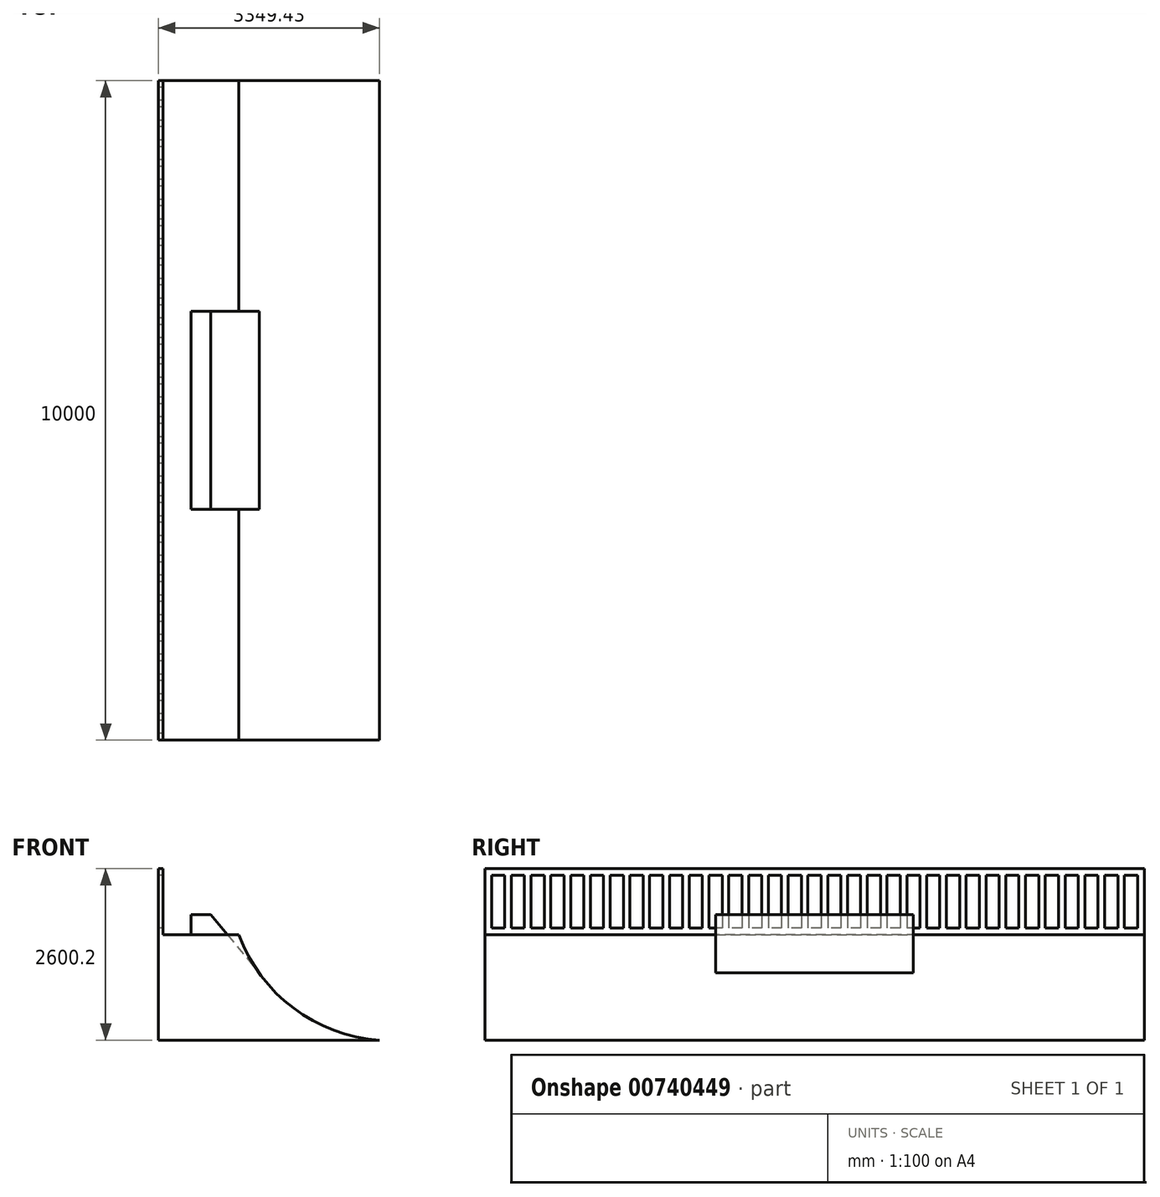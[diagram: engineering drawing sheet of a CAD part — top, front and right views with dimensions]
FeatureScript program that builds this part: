
annotation { "Feature Type Name" : "Feature", "Feature Type Description" : "" }
export const myFeature = defineFeature(function(context is Context, id is Id, definition is map)
    precondition{}
    {
        {
            var Q0;
            Q0=qCreatedBy(makeId("Top.planeOp"),FACE);
            var sketch = newSketch(context, id + "F0", { "sketchPlane" : qUnion([Q0])});
            skLineSegment(sketch, "E0.bottom", {"start": v(5000, 5000) * mm, "end": v(-5000, 5000) * mm, "construction": true});
            skLineSegment(sketch, "E0.top", {"start": v(5000, -5000) * mm, "end": v(-5000, -5000) * mm, "construction": true});
            skLineSegment(sketch, "E0.left", {"start": v(5000, 5000) * mm, "end": v(5000, -5000) * mm, "construction": true});
            skLineSegment(sketch, "E0.right", {"start": v(-5000, 5000) * mm, "end": v(-5000, -5000) * mm});
            skPoint(sketch, "E0.middle", {"position": v(0, 0) * mm});
            skLineSegment(sketch, "E1", {"start": v(-3780.8, 5000) * mm, "end": v(-3780.8, -5000) * mm});
            skLineSegment(sketch, "E2", {"start": v(-3780.8, -5000) * mm, "end": v(-5000, -5000) * mm});
            skLineSegment(sketch, "E3", {"start": v(-3780.8, 5000) * mm, "end": v(-5000, 5000) * mm});
            skSolve(sketch);
        }
        {
            var Q0;
            Q0=makeQuery(id+"F0.imprint","IMPRINT",FACE,{"disambiguationData":[TD([[makeQuery(id+"F0.imprint","IMPRINT",EDGE,{"derivedFrom":sQuery(id+"F0.wireOp",EDGE,"E0.right")}),1.0]])]});
            extrude(context, id + "F1", {"entities" : qUnion([Q0]), "depth" : 1600.2 * mm, "offsetDistance" : 25 * mm});
        }
        {
            var Q0;
            Q0=makeQuery(id+"F1.opExtrude","SWEPT_FACE",FACE,{"disambiguationData":[OSD([sQuery(id+"F0.wireOp",EDGE,"E2")])]});
            var sketch = newSketch(context, id + "F2", { "sketchPlane" : qUnion([Q0])});
            skLineSegment(sketch, "E4.0", {"start": v(-3780.8, 1600.2) * mm, "end": v(-3780.8, 0) * mm});
            skLineSegment(sketch, "E5", {"start": v(-3780.8, 0) * mm, "end": v(-365.8, 0) * mm});
            skLineSegment(sketch, "E6", {"start": v(-3994.4, 2438.4) * mm, "end": v(213.94, 2438.4) * mm, "construction": true});
            skArc(sketch, "E7", {"start": v(-3780.8, 1600.2) * mm, "mid": v(-2821.2, 390.7) * mm, "end": v(-1327.5, 0) * mm});
            skLineSegment(sketch, "E8", {"start": v(-3780.8, 1600.2) * mm, "end": v(-3655.75, 1314.5) * mm, "construction": true});
            skLineSegment(sketch, "E9.0", {"start": v(-3780.8, 1600.2) * mm, "end": v(-5000, 1600.2) * mm});
            skSolve(sketch);
        }
        {
            var Q0;
            {var subQ0=sQuery(id+"F2.wireOp",EDGE,"E4.0");Q0=makeQuery(id+"F2.imprint","IMPRINT",FACE,{"disambiguationData":[TD([[makeQuery(id+"F2.imprint","IMPRINT",EDGE,{"derivedFrom":subQ0}),1.0]])]});}
            var Q1;
            Q1=makeQuery(id+"F1.opExtrude","CAP_EDGE",EDGE,{"disambiguationData":[OSD([sQuery(id+"F0.wireOp",EDGE,"E1")])],"isStart":false});
            sweep(context, id + "F3", {"operationType" : NewBodyOperationType.ADD, "profiles" : qUnion([Q0]), "path" : qUnion([Q1])});
        }
        {
            var Q0;
            Q0=makeQuery(id+"F1.opExtrude","SWEPT_FACE",FACE,{"disambiguationData":[OSD([sQuery(id+"F0.wireOp",EDGE,"E0.right")])]});
            var sketch = newSketch(context, id + "F4", { "sketchPlane" : qUnion([Q0])});
            skLineSegment(sketch, "E10.0", {"start": v(-5000, 1600.2) * mm, "end": v(5000, 1600.2) * mm});
            skLineSegment(sketch, "E11.top", {"start": v(-5000, 2600.2) * mm, "end": v(5000, 2600.2) * mm});
            skLineSegment(sketch, "E11.left", {"start": v(-5000, 1600.2) * mm, "end": v(-5000, 2600.2) * mm});
            skLineSegment(sketch, "E11.right", {"start": v(5000, 1600.2) * mm, "end": v(5000, 2600.2) * mm});
            skLineSegment(sketch, "E12.bottom", {"start": v(-4900, 2500.2) * mm, "end": v(-4700, 2500.2) * mm});
            skLineSegment(sketch, "E12.top", {"start": v(-4900, 1700.2) * mm, "end": v(-4700, 1700.2) * mm});
            skLineSegment(sketch, "E12.left", {"start": v(-4900, 2500.2) * mm, "end": v(-4900, 1700.2) * mm});
            skLineSegment(sketch, "E12.right", {"start": v(-4700, 2500.2) * mm, "end": v(-4700, 1700.2) * mm});
            skLineSegment(sketch, "E13.1.0.0", {"start": v(-4400, 2500.2) * mm, "end": v(-4400, 1700.2) * mm});
            skLineSegment(sketch, "E13.1.0.1", {"start": v(-4600, 2500.2) * mm, "end": v(-4400, 2500.2) * mm});
            skLineSegment(sketch, "E13.1.0.2", {"start": v(-4600, 2500.2) * mm, "end": v(-4600, 1700.2) * mm});
            skLineSegment(sketch, "E13.1.0.3", {"start": v(-4600, 1700.2) * mm, "end": v(-4400, 1700.2) * mm});
            skLineSegment(sketch, "E13.2.0.0", {"start": v(-4100, 2500.2) * mm, "end": v(-4100, 1700.2) * mm});
            skLineSegment(sketch, "E13.2.0.1", {"start": v(-4300, 2500.2) * mm, "end": v(-4100, 2500.2) * mm});
            skLineSegment(sketch, "E13.2.0.2", {"start": v(-4300, 2500.2) * mm, "end": v(-4300, 1700.2) * mm});
            skLineSegment(sketch, "E13.2.0.3", {"start": v(-4300, 1700.2) * mm, "end": v(-4100, 1700.2) * mm});
            skLineSegment(sketch, "E13.3.0.0", {"start": v(-3800, 2500.2) * mm, "end": v(-3800, 1700.2) * mm});
            skLineSegment(sketch, "E13.3.0.1", {"start": v(-4000, 2500.2) * mm, "end": v(-3800, 2500.2) * mm});
            skLineSegment(sketch, "E13.3.0.2", {"start": v(-4000, 2500.2) * mm, "end": v(-4000, 1700.2) * mm});
            skLineSegment(sketch, "E13.3.0.3", {"start": v(-4000, 1700.2) * mm, "end": v(-3800, 1700.2) * mm});
            skLineSegment(sketch, "E13.4.0.0", {"start": v(-3500, 2500.2) * mm, "end": v(-3500, 1700.2) * mm});
            skLineSegment(sketch, "E13.4.0.1", {"start": v(-3700, 2500.2) * mm, "end": v(-3500, 2500.2) * mm});
            skLineSegment(sketch, "E13.4.0.2", {"start": v(-3700, 2500.2) * mm, "end": v(-3700, 1700.2) * mm});
            skLineSegment(sketch, "E13.4.0.3", {"start": v(-3700, 1700.2) * mm, "end": v(-3500, 1700.2) * mm});
            skLineSegment(sketch, "E13.5.0.0", {"start": v(-3200, 2500.2) * mm, "end": v(-3200, 1700.2) * mm});
            skLineSegment(sketch, "E13.5.0.1", {"start": v(-3400, 2500.2) * mm, "end": v(-3200, 2500.2) * mm});
            skLineSegment(sketch, "E13.5.0.2", {"start": v(-3400, 2500.2) * mm, "end": v(-3400, 1700.2) * mm});
            skLineSegment(sketch, "E13.5.0.3", {"start": v(-3400, 1700.2) * mm, "end": v(-3200, 1700.2) * mm});
            skLineSegment(sketch, "E13.6.0.0", {"start": v(-2900, 2500.2) * mm, "end": v(-2900, 1700.2) * mm});
            skLineSegment(sketch, "E13.6.0.1", {"start": v(-3100, 2500.2) * mm, "end": v(-2900, 2500.2) * mm});
            skLineSegment(sketch, "E13.6.0.2", {"start": v(-3100, 2500.2) * mm, "end": v(-3100, 1700.2) * mm});
            skLineSegment(sketch, "E13.6.0.3", {"start": v(-3100, 1700.2) * mm, "end": v(-2900, 1700.2) * mm});
            skLineSegment(sketch, "E13.7.0.0", {"start": v(-2600, 2500.2) * mm, "end": v(-2600, 1700.2) * mm});
            skLineSegment(sketch, "E13.7.0.1", {"start": v(-2800, 2500.2) * mm, "end": v(-2600, 2500.2) * mm});
            skLineSegment(sketch, "E13.7.0.2", {"start": v(-2800, 2500.2) * mm, "end": v(-2800, 1700.2) * mm});
            skLineSegment(sketch, "E13.7.0.3", {"start": v(-2800, 1700.2) * mm, "end": v(-2600, 1700.2) * mm});
            skLineSegment(sketch, "E13.8.0.0", {"start": v(-2300, 2500.2) * mm, "end": v(-2300, 1700.2) * mm});
            skLineSegment(sketch, "E13.8.0.1", {"start": v(-2500, 2500.2) * mm, "end": v(-2300, 2500.2) * mm});
            skLineSegment(sketch, "E13.8.0.2", {"start": v(-2500, 2500.2) * mm, "end": v(-2500, 1700.2) * mm});
            skLineSegment(sketch, "E13.8.0.3", {"start": v(-2500, 1700.2) * mm, "end": v(-2300, 1700.2) * mm});
            skLineSegment(sketch, "E13.9.0.0", {"start": v(-2000, 2500.2) * mm, "end": v(-2000, 1700.2) * mm});
            skLineSegment(sketch, "E13.9.0.1", {"start": v(-2200, 2500.2) * mm, "end": v(-2000, 2500.2) * mm});
            skLineSegment(sketch, "E13.9.0.2", {"start": v(-2200, 2500.2) * mm, "end": v(-2200, 1700.2) * mm});
            skLineSegment(sketch, "E13.9.0.3", {"start": v(-2200, 1700.2) * mm, "end": v(-2000, 1700.2) * mm});
            skLineSegment(sketch, "E13.10.0.0", {"start": v(-1700, 2500.2) * mm, "end": v(-1700, 1700.2) * mm});
            skLineSegment(sketch, "E13.10.0.1", {"start": v(-1900, 2500.2) * mm, "end": v(-1700, 2500.2) * mm});
            skLineSegment(sketch, "E13.10.0.2", {"start": v(-1900, 2500.2) * mm, "end": v(-1900, 1700.2) * mm});
            skLineSegment(sketch, "E13.10.0.3", {"start": v(-1900, 1700.2) * mm, "end": v(-1700, 1700.2) * mm});
            skLineSegment(sketch, "E13.11.0.0", {"start": v(-1400, 2500.2) * mm, "end": v(-1400, 1700.2) * mm});
            skLineSegment(sketch, "E13.11.0.1", {"start": v(-1600, 2500.2) * mm, "end": v(-1400, 2500.2) * mm});
            skLineSegment(sketch, "E13.11.0.2", {"start": v(-1600, 2500.2) * mm, "end": v(-1600, 1700.2) * mm});
            skLineSegment(sketch, "E13.11.0.3", {"start": v(-1600, 1700.2) * mm, "end": v(-1400, 1700.2) * mm});
            skLineSegment(sketch, "E13.12.0.0", {"start": v(-1100, 2500.2) * mm, "end": v(-1100, 1700.2) * mm});
            skLineSegment(sketch, "E13.12.0.1", {"start": v(-1300, 2500.2) * mm, "end": v(-1100, 2500.2) * mm});
            skLineSegment(sketch, "E13.12.0.2", {"start": v(-1300, 2500.2) * mm, "end": v(-1300, 1700.2) * mm});
            skLineSegment(sketch, "E13.12.0.3", {"start": v(-1300, 1700.2) * mm, "end": v(-1100, 1700.2) * mm});
            skLineSegment(sketch, "E13.13.0.0", {"start": v(-800, 2500.2) * mm, "end": v(-800, 1700.2) * mm});
            skLineSegment(sketch, "E13.13.0.1", {"start": v(-1000, 2500.2) * mm, "end": v(-800, 2500.2) * mm});
            skLineSegment(sketch, "E13.13.0.2", {"start": v(-1000, 2500.2) * mm, "end": v(-1000, 1700.2) * mm});
            skLineSegment(sketch, "E13.13.0.3", {"start": v(-1000, 1700.2) * mm, "end": v(-800, 1700.2) * mm});
            skLineSegment(sketch, "E13.14.0.0", {"start": v(-500, 2500.2) * mm, "end": v(-500, 1700.2) * mm});
            skLineSegment(sketch, "E13.14.0.1", {"start": v(-700, 2500.2) * mm, "end": v(-500, 2500.2) * mm});
            skLineSegment(sketch, "E13.14.0.2", {"start": v(-700, 2500.2) * mm, "end": v(-700, 1700.2) * mm});
            skLineSegment(sketch, "E13.14.0.3", {"start": v(-700, 1700.2) * mm, "end": v(-500, 1700.2) * mm});
            skLineSegment(sketch, "E13.15.0.0", {"start": v(-200, 2500.2) * mm, "end": v(-200, 1700.2) * mm});
            skLineSegment(sketch, "E13.15.0.1", {"start": v(-400, 2500.2) * mm, "end": v(-200, 2500.2) * mm});
            skLineSegment(sketch, "E13.15.0.2", {"start": v(-400, 2500.2) * mm, "end": v(-400, 1700.2) * mm});
            skLineSegment(sketch, "E13.15.0.3", {"start": v(-400, 1700.2) * mm, "end": v(-200, 1700.2) * mm});
            skLineSegment(sketch, "E13.16.0.0", {"start": v(100, 2500.2) * mm, "end": v(100, 1700.2) * mm});
            skLineSegment(sketch, "E13.16.0.1", {"start": v(-100, 2500.2) * mm, "end": v(100, 2500.2) * mm});
            skLineSegment(sketch, "E13.16.0.2", {"start": v(-100, 2500.2) * mm, "end": v(-100, 1700.2) * mm});
            skLineSegment(sketch, "E13.16.0.3", {"start": v(-100, 1700.2) * mm, "end": v(100, 1700.2) * mm});
            skLineSegment(sketch, "E13.17.0.0", {"start": v(400, 2500.2) * mm, "end": v(400, 1700.2) * mm});
            skLineSegment(sketch, "E13.17.0.1", {"start": v(200, 2500.2) * mm, "end": v(400, 2500.2) * mm});
            skLineSegment(sketch, "E13.17.0.2", {"start": v(200, 2500.2) * mm, "end": v(200, 1700.2) * mm});
            skLineSegment(sketch, "E13.17.0.3", {"start": v(200, 1700.2) * mm, "end": v(400, 1700.2) * mm});
            skLineSegment(sketch, "E13.18.0.0", {"start": v(700, 2500.2) * mm, "end": v(700, 1700.2) * mm});
            skLineSegment(sketch, "E13.18.0.1", {"start": v(500, 2500.2) * mm, "end": v(700, 2500.2) * mm});
            skLineSegment(sketch, "E13.18.0.2", {"start": v(500, 2500.2) * mm, "end": v(500, 1700.2) * mm});
            skLineSegment(sketch, "E13.18.0.3", {"start": v(500, 1700.2) * mm, "end": v(700, 1700.2) * mm});
            skLineSegment(sketch, "E13.19.0.0", {"start": v(1000, 2500.2) * mm, "end": v(1000, 1700.2) * mm});
            skLineSegment(sketch, "E13.19.0.1", {"start": v(800, 2500.2) * mm, "end": v(1000, 2500.2) * mm});
            skLineSegment(sketch, "E13.19.0.2", {"start": v(800, 2500.2) * mm, "end": v(800, 1700.2) * mm});
            skLineSegment(sketch, "E13.19.0.3", {"start": v(800, 1700.2) * mm, "end": v(1000, 1700.2) * mm});
            skLineSegment(sketch, "E13.20.0.0", {"start": v(1300, 2500.2) * mm, "end": v(1300, 1700.2) * mm});
            skLineSegment(sketch, "E13.20.0.1", {"start": v(1100, 2500.2) * mm, "end": v(1300, 2500.2) * mm});
            skLineSegment(sketch, "E13.20.0.2", {"start": v(1100, 2500.2) * mm, "end": v(1100, 1700.2) * mm});
            skLineSegment(sketch, "E13.20.0.3", {"start": v(1100, 1700.2) * mm, "end": v(1300, 1700.2) * mm});
            skLineSegment(sketch, "E13.21.0.0", {"start": v(1600, 2500.2) * mm, "end": v(1600, 1700.2) * mm});
            skLineSegment(sketch, "E13.21.0.1", {"start": v(1400, 2500.2) * mm, "end": v(1600, 2500.2) * mm});
            skLineSegment(sketch, "E13.21.0.2", {"start": v(1400, 2500.2) * mm, "end": v(1400, 1700.2) * mm});
            skLineSegment(sketch, "E13.21.0.3", {"start": v(1400, 1700.2) * mm, "end": v(1600, 1700.2) * mm});
            skLineSegment(sketch, "E13.22.0.0", {"start": v(1900, 2500.2) * mm, "end": v(1900, 1700.2) * mm});
            skLineSegment(sketch, "E13.22.0.1", {"start": v(1700, 2500.2) * mm, "end": v(1900, 2500.2) * mm});
            skLineSegment(sketch, "E13.22.0.2", {"start": v(1700, 2500.2) * mm, "end": v(1700, 1700.2) * mm});
            skLineSegment(sketch, "E13.22.0.3", {"start": v(1700, 1700.2) * mm, "end": v(1900, 1700.2) * mm});
            skLineSegment(sketch, "E13.23.0.0", {"start": v(2200, 2500.2) * mm, "end": v(2200, 1700.2) * mm});
            skLineSegment(sketch, "E13.23.0.1", {"start": v(2000, 2500.2) * mm, "end": v(2200, 2500.2) * mm});
            skLineSegment(sketch, "E13.23.0.2", {"start": v(2000, 2500.2) * mm, "end": v(2000, 1700.2) * mm});
            skLineSegment(sketch, "E13.23.0.3", {"start": v(2000, 1700.2) * mm, "end": v(2200, 1700.2) * mm});
            skLineSegment(sketch, "E13.24.0.0", {"start": v(2500, 2500.2) * mm, "end": v(2500, 1700.2) * mm});
            skLineSegment(sketch, "E13.24.0.1", {"start": v(2300, 2500.2) * mm, "end": v(2500, 2500.2) * mm});
            skLineSegment(sketch, "E13.24.0.2", {"start": v(2300, 2500.2) * mm, "end": v(2300, 1700.2) * mm});
            skLineSegment(sketch, "E13.24.0.3", {"start": v(2300, 1700.2) * mm, "end": v(2500, 1700.2) * mm});
            skLineSegment(sketch, "E13.direction1", {"start": v(-4700, 1700.2) * mm, "end": v(-4400, 1700.2) * mm, "construction": true});
            skLineSegment(sketch, "E14.0.25.0", {"start": v(2800, 2500.2) * mm, "end": v(2800, 1700.2) * mm});
            skLineSegment(sketch, "E14.3.25.0", {"start": v(2600, 2500.2) * mm, "end": v(2800, 2500.2) * mm});
            skLineSegment(sketch, "E14.6.25.0", {"start": v(2600, 2500.2) * mm, "end": v(2600, 1700.2) * mm});
            skLineSegment(sketch, "E14.9.25.0", {"start": v(2600, 1700.2) * mm, "end": v(2800, 1700.2) * mm});
            skLineSegment(sketch, "E14.0.26.0", {"start": v(3100, 2500.2) * mm, "end": v(3100, 1700.2) * mm});
            skLineSegment(sketch, "E14.3.26.0", {"start": v(2900, 2500.2) * mm, "end": v(3100, 2500.2) * mm});
            skLineSegment(sketch, "E14.6.26.0", {"start": v(2900, 2500.2) * mm, "end": v(2900, 1700.2) * mm});
            skLineSegment(sketch, "E14.9.26.0", {"start": v(2900, 1700.2) * mm, "end": v(3100, 1700.2) * mm});
            skLineSegment(sketch, "E14.0.27.0", {"start": v(3400, 2500.2) * mm, "end": v(3400, 1700.2) * mm});
            skLineSegment(sketch, "E14.3.27.0", {"start": v(3200, 2500.2) * mm, "end": v(3400, 2500.2) * mm});
            skLineSegment(sketch, "E14.6.27.0", {"start": v(3200, 2500.2) * mm, "end": v(3200, 1700.2) * mm});
            skLineSegment(sketch, "E14.9.27.0", {"start": v(3200, 1700.2) * mm, "end": v(3400, 1700.2) * mm});
            skLineSegment(sketch, "E14.0.28.0", {"start": v(3700, 2500.2) * mm, "end": v(3700, 1700.2) * mm});
            skLineSegment(sketch, "E14.3.28.0", {"start": v(3500, 2500.2) * mm, "end": v(3700, 2500.2) * mm});
            skLineSegment(sketch, "E14.6.28.0", {"start": v(3500, 2500.2) * mm, "end": v(3500, 1700.2) * mm});
            skLineSegment(sketch, "E14.9.28.0", {"start": v(3500, 1700.2) * mm, "end": v(3700, 1700.2) * mm});
            skLineSegment(sketch, "E14.0.29.0", {"start": v(4000, 2500.2) * mm, "end": v(4000, 1700.2) * mm});
            skLineSegment(sketch, "E14.3.29.0", {"start": v(3800, 2500.2) * mm, "end": v(4000, 2500.2) * mm});
            skLineSegment(sketch, "E14.6.29.0", {"start": v(3800, 2500.2) * mm, "end": v(3800, 1700.2) * mm});
            skLineSegment(sketch, "E14.9.29.0", {"start": v(3800, 1700.2) * mm, "end": v(4000, 1700.2) * mm});
            skLineSegment(sketch, "E14.0.30.0", {"start": v(4300, 2500.2) * mm, "end": v(4300, 1700.2) * mm});
            skLineSegment(sketch, "E14.3.30.0", {"start": v(4100, 2500.2) * mm, "end": v(4300, 2500.2) * mm});
            skLineSegment(sketch, "E14.6.30.0", {"start": v(4100, 2500.2) * mm, "end": v(4100, 1700.2) * mm});
            skLineSegment(sketch, "E14.9.30.0", {"start": v(4100, 1700.2) * mm, "end": v(4300, 1700.2) * mm});
            skLineSegment(sketch, "E14.0.31.0", {"start": v(4600, 2500.2) * mm, "end": v(4600, 1700.2) * mm});
            skLineSegment(sketch, "E14.3.31.0", {"start": v(4400, 2500.2) * mm, "end": v(4600, 2500.2) * mm});
            skLineSegment(sketch, "E14.6.31.0", {"start": v(4400, 2500.2) * mm, "end": v(4400, 1700.2) * mm});
            skLineSegment(sketch, "E14.9.31.0", {"start": v(4400, 1700.2) * mm, "end": v(4600, 1700.2) * mm});
            skLineSegment(sketch, "E14.0.32.0", {"start": v(4900, 2500.2) * mm, "end": v(4900, 1700.2) * mm});
            skLineSegment(sketch, "E14.3.32.0", {"start": v(4700, 2500.2) * mm, "end": v(4900, 2500.2) * mm});
            skLineSegment(sketch, "E14.6.32.0", {"start": v(4700, 2500.2) * mm, "end": v(4700, 1700.2) * mm});
            skLineSegment(sketch, "E14.9.32.0", {"start": v(4700, 1700.2) * mm, "end": v(4900, 1700.2) * mm});
            skSolve(sketch);
        }
        {
            var Q0;
            Q0=makeQuery(id+"F4.imprint","IMPRINT",FACE,{"disambiguationData":[TD([[makeQuery(id+"F4.imprint","IMPRINT",EDGE,{"derivedFrom":sQuery(id+"F4.wireOp",EDGE,"E10.0")}),1.0]])]});
            extrude(context, id + "F5", {"entities" : qUnion([Q0]), "operationType" : NewBodyOperationType.ADD, "oppositeDirection" : true, "depth" : 70 * mm, "offsetDistance" : 25 * mm});
        }
        {
            var Q0;
            {var subQ0=sQuery(id+"F0.wireOp",EDGE,"E1");Q0=makeQuery(id+"F3.boolean.opBoolean","MERGE",EDGE,{"derivedFrom":[makeQuery(id+"F1.opExtrude","CAP_EDGE",EDGE,{"disambiguationData":[OSD([subQ0])],"isStart":false}),makeQuery(id+"F3.opSweep","SWEPT_EDGE",EDGE,{"disambiguationData":[OSD([subQ0,sQuery(id+"F2.wireOp",EDGE,"E4.0"),sQuery(id+"F2.wireOp",EDGE,"E7"),sQuery(id+"F2.wireOp",EDGE,"E9.0")])]})]});}
            cPoint(context, id + "F6", {"entities" : qUnion([Q0]), "parameter" : 0.5});
        }
        {
            var Q0;
            Q0 = qCreatedBy(id + "F6" ,VERTEX);
            var Q1;
            {var subQ0=sQuery(id+"F0.wireOp",EDGE,"E1");Q1=makeQuery(id+"F3.boolean.opBoolean","MERGE",EDGE,{"derivedFrom":[makeQuery(id+"F1.opExtrude","CAP_EDGE",EDGE,{"disambiguationData":[OSD([subQ0])],"isStart":false}),makeQuery(id+"F3.opSweep","SWEPT_EDGE",EDGE,{"disambiguationData":[OSD([subQ0,sQuery(id+"F2.wireOp",EDGE,"E4.0"),sQuery(id+"F2.wireOp",EDGE,"E7"),sQuery(id+"F2.wireOp",EDGE,"E9.0")])]})]});}
            cPlane(context, id + "F7", {"entities" : qUnion([Q0, Q1]), "cplaneType" : CPlaneType.LINE_POINT, "offset" : 25 * mm, "width" : 150 * mm, "height" : 150 * mm});
        }
        {
            var Q0;
            Q0=qCreatedBy(id+"F7.planeOp",FACE);
            var sketch = newSketch(context, id + "F8", { "sketchPlane" : qUnion([Q0])});
            skLineSegment(sketch, "E15.0", {"start": v(-3780.8, 1600.2) * mm, "end": v(-4930, 1600.2) * mm});
            skLineSegment(sketch, "E16", {"start": v(-4505.29, 1900.2) * mm, "end": v(-4205.29, 1900.2) * mm});
            skLineSegment(sketch, "E17", {"start": v(-4205.29, 1900.2) * mm, "end": v(-3334.45, 848.31) * mm});
            skLineSegment(sketch, "E18", {"start": v(-3334.45, 848.31) * mm, "end": v(-3353.28, 1927.1) * mm});
            skLineSegment(sketch, "E19", {"start": v(-3353.28, 1927.1) * mm, "end": v(-4205.29, 1900.2) * mm});
            skLineSegment(sketch, "E20", {"start": v(-4505.29, 1900.2) * mm, "end": v(-4505.29, 1600.2) * mm});
            skSolve(sketch);
        }
        {
            var Q0;
            {var subQ4=sQuery(id+"F8.wireOp",EDGE,"E16");Q0=makeQuery(id+"F8.imprint","IMPRINT",FACE,{"disambiguationData":[TD([[makeQuery(id+"F8.imprint","IMPRINT",EDGE,{"derivedFrom":subQ4}),-1.0]])]});}
            extrude(context, id + "F9", {"entities" : qUnion([Q0]), "operationType" : NewBodyOperationType.ADD, "depth" : 3000 * mm, "offsetDistance" : 25 * mm, "symmetric" : true});
        }
        {
            var Q0;
            {var subQ3=sQuery(id+"F8.wireOp",EDGE,"E18");Q0=makeQuery(id+"F8.imprint","IMPRINT",FACE,{"disambiguationData":[TD([[makeQuery(id+"F8.imprint","IMPRINT",EDGE,{"derivedFrom":subQ3}),1.0]])]});}
            extrude(context, id + "F10", {"entities" : qUnion([Q0]), "operationType" : NewBodyOperationType.REMOVE, "depth" : 3000 * mm, "offsetDistance" : 25 * mm, "symmetric" : true});
        }
    });
